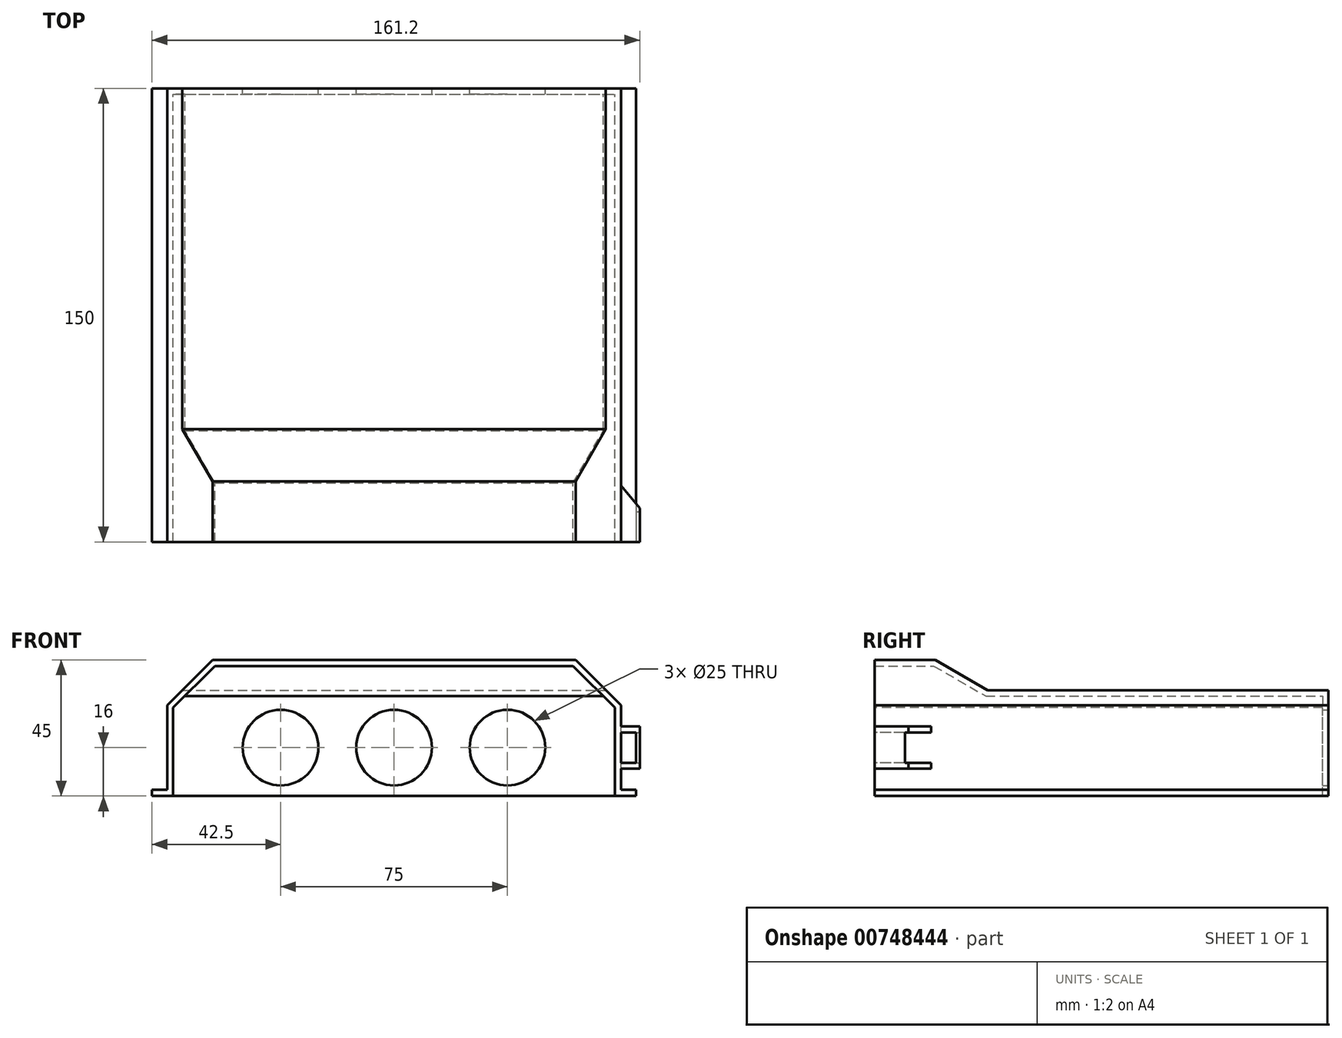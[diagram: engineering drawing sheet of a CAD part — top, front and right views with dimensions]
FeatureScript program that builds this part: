
annotation { "Feature Type Name" : "Feature", "Feature Type Description" : "" }
export const myFeature = defineFeature(function(context is Context, id is Id, definition is map)
    precondition{}
    {
        {
            var Q0;
            Q0=qCreatedBy(makeId("Front.planeOp"),FACE);
            var sketch = newSketch(context, id + "F0", { "sketchPlane" : qUnion([Q0])});
            skLineSegment(sketch, "E0.bottom", {"start": v(0, 0) * mm, "end": v(150, 0) * mm});
            skLineSegment(sketch, "E0.top", {"start": v(0, 45) * mm, "end": v(150, 45) * mm});
            skLineSegment(sketch, "E0.left", {"start": v(0, 0) * mm, "end": v(0, 45) * mm});
            skLineSegment(sketch, "E0.right", {"start": v(150, 0) * mm, "end": v(150, 45) * mm});
            skSolve(sketch);
        }
        {
            var Q0;
            Q0=qSketchRegion(id+"F0",true);
            extrude(context, id + "F1", {"entities" : qUnion([Q0]), "depth" : 150 * mm, "offsetDistance" : 25 * mm});
        }
        {
            var Q0;
            Q0=makeQuery(id+"F1.opExtrude","SWEPT_FACE",FACE,{"disambiguationData":[OSD([sQuery(id+"F0.wireOp",EDGE,"E0.bottom")])]});
            var sketch = newSketch(context, id + "F2", { "sketchPlane" : qUnion([Q0])});
            skLineSegment(sketch, "E1.0", {"start": v(150, 150) * mm, "end": v(150, 0) * mm});
            skLineSegment(sketch, "E2.0", {"start": v(0, 150) * mm, "end": v(0, 0) * mm});
            skLineSegment(sketch, "E3", {"start": v(0, 150) * mm, "end": v(-5, 150) * mm});
            skLineSegment(sketch, "E4", {"start": v(-5, 150) * mm, "end": v(-5, 0) * mm});
            skLineSegment(sketch, "E5", {"start": v(155, 0) * mm, "end": v(155, 150) * mm});
            skLineSegment(sketch, "E6", {"start": v(155, 150) * mm, "end": v(150, 150) * mm});
            skLineSegment(sketch, "E7", {"start": v(150, 0) * mm, "end": v(155, 0) * mm});
            skLineSegment(sketch, "E8", {"start": v(0.46, 0) * mm, "end": v(-5, 0) * mm});
            skSolve(sketch);
        }
        {
            var Q0;
            Q0=makeQuery(id+"F2.imprint","IMPRINT",FACE,{"disambiguationData":[TD([[makeQuery(id+"F2.imprint","IMPRINT",EDGE,{"derivedFrom":sQuery(id+"F2.wireOp",EDGE,"E1.0")}),1.0]])]});
            var Q1;
            {var subQ0=sQuery(id+"F2.wireOp",EDGE,"E2.0");Q1=makeQuery(id+"F2.imprint","IMPRINT",FACE,{"disambiguationData":[TD([[makeQuery(id+"F2.imprint","IMPRINT",EDGE,{"derivedFrom":subQ0}),-1.0]])]});}
            extrude(context, id + "F3", {"entities" : qUnion([Q0, Q1]), "operationType" : NewBodyOperationType.ADD, "oppositeDirection" : true, "depth" : 2 * mm, "offsetDistance" : 25 * mm});
        }
        {
            var Q0;
            Q0=makeQuery(id+"F1.opExtrude","SWEPT_FACE",FACE,{"disambiguationData":[OSD([sQuery(id+"F0.wireOp",EDGE,"E0.right")])]});
            var sketch = newSketch(context, id + "F4", { "sketchPlane" : qUnion([Q0])});
            skLineSegment(sketch, "E9", {"start": v(0, 45) * mm, "end": v(-130, 45) * mm});
            skLineSegment(sketch, "E10", {"start": v(-130, 45) * mm, "end": v(-112.68, 35) * mm});
            skLineSegment(sketch, "E11", {"start": v(-112.68, 35) * mm, "end": v(0, 35) * mm});
            skLineSegment(sketch, "E12", {"start": v(0, 35) * mm, "end": v(0, 45) * mm});
            skSolve(sketch);
        }
        {
            var Q0;
            Q0 = qSketchRegion(id + "F4", true);
            extrude(context, id + "F5", {"entities" : qUnion([Q0]), "operationType" : NewBodyOperationType.REMOVE, "endBound" : BoundingType.UP_TO_NEXT, "oppositeDirection" : true, "depth" : 25 * mm, "offsetDistance" : 25 * mm});
        }
        {
            var Q0;
            Q0=makeQuery(id+"FCt8RxKQ0T1Ob7Y_1.boolean.opBoolean","COPY",EDGE,{"derivedFrom":makeQuery(id+"FCt8RxKQ0T1Ob7Y_1.opExtrude","SWEPT_EDGE",EDGE,{"disambiguationData":[OSD([sQuery(id+"FIqywhC7vN5m6TC_1.wireOp",EDGE,"XllLzcVL-DN8Z-CTJ4-3NpV-jDezmlgxU65w.top"),sQuery(id+"FIqywhC7vN5m6TC_1.wireOp",EDGE,"XllLzcVL-DN8Z-CTJ4-3NpV-jDezmlgxU65w.left")])]})});
            var Q1;
            Q1=makeQuery(id+"FCt8RxKQ0T1Ob7Y_1.boolean.opBoolean","COPY",EDGE,{"derivedFrom":makeQuery(id+"FCt8RxKQ0T1Ob7Y_1.opExtrude","TWEAK_EDGE",EDGE,{"derivedFrom":[makeQuery(id+"F1.opExtrude","CAP_FACE",FACE,{"disambiguationData":[OSD([sQuery(id+"F0.wireOp",EDGE,"E0.bottom"),sQuery(id+"F0.wireOp",EDGE,"E0.top"),sQuery(id+"F0.wireOp",EDGE,"E0.left"),sQuery(id+"F0.wireOp",EDGE,"E0.right")])],"isStart":true}),makeQuery(id+"FIqywhC7vN5m6TC_1.imprint","IMPRINT",EDGE,{"derivedFrom":sQuery(id+"FIqywhC7vN5m6TC_1.wireOp",EDGE,"XllLzcVL-DN8Z-CTJ4-3NpV-jDezmlgxU65w.top")})]})});
            var Q2;
            Q2=makeQuery(id+"FCt8RxKQ0T1Ob7Y_1.boolean.opBoolean","COPY",EDGE,{"derivedFrom":makeQuery(id+"FCt8RxKQ0T1Ob7Y_1.opExtrude","SWEPT_EDGE",EDGE,{"disambiguationData":[OSD([sQuery(id+"FIqywhC7vN5m6TC_1.wireOp",EDGE,"XllLzcVL-DN8Z-CTJ4-3NpV-jDezmlgxU65w.top"),sQuery(id+"FIqywhC7vN5m6TC_1.wireOp",EDGE,"XllLzcVL-DN8Z-CTJ4-3NpV-jDezmlgxU65w.right")])]})});
            var Q3;
            Q3=makeQuery(id+"F1.opExtrude","SWEPT_EDGE",EDGE,{"disambiguationData":[OSD([sQuery(id+"F0.wireOp",EDGE,"E0.top"),sQuery(id+"F0.wireOp",EDGE,"E0.left")])]});
            var Q4;
            Q4=makeQuery(id+"F1.opExtrude","CAP_EDGE",EDGE,{"disambiguationData":[OSD([sQuery(id+"F0.wireOp",EDGE,"E0.top")])],"isStart":true});
            var Q5;
            Q5=makeQuery(id+"F1.opExtrude","SWEPT_EDGE",EDGE,{"disambiguationData":[OSD([sQuery(id+"F0.wireOp",EDGE,"E0.top"),sQuery(id+"F0.wireOp",EDGE,"E0.right")])]});
            chamfer(context, id + "F6", {"entities" : qUnion([Q0, Q1, Q2, Q3, Q4, Q5]), "width" : 15 * mm, "tangentPropagation" : true});
        }
        {
            var Q0;
            Q0=makeQuery(id+"F3.boolean.opBoolean","MERGE",FACE,{"derivedFrom":[makeQuery(id+"F1.opExtrude","CAP_FACE",FACE,{"disambiguationData":[OSD([sQuery(id+"F0.wireOp",EDGE,"E0.bottom"),sQuery(id+"F0.wireOp",EDGE,"E0.top"),sQuery(id+"F0.wireOp",EDGE,"E0.left"),sQuery(id+"F0.wireOp",EDGE,"E0.right")])],"isStart":false}),makeQuery(id+"F3.opExtrude","SWEPT_FACE",FACE,{"disambiguationData":[OSD([sQuery(id+"F2.wireOp",EDGE,"E3")])]}),makeQuery(id+"F3.opExtrude","SWEPT_FACE",FACE,{"disambiguationData":[OSD([sQuery(id+"F2.wireOp",EDGE,"E6")])]})]});
            var Q1;
            Q1=makeQuery(id+"F3.boolean.opBoolean","MERGE",FACE,{"derivedFrom":[makeQuery(id+"F1.opExtrude","SWEPT_FACE",FACE,{"disambiguationData":[OSD([sQuery(id+"F0.wireOp",EDGE,"E0.bottom")])]}),makeQuery(id+"F3.opExtrude","CAP_FACE",FACE,{"disambiguationData":[OSD([sQuery(id+"F2.wireOp",EDGE,"E1.0"),sQuery(id+"F2.wireOp",EDGE,"E5"),sQuery(id+"F2.wireOp",EDGE,"E6"),sQuery(id+"F2.wireOp",EDGE,"E7")])],"isStart":true}),makeQuery(id+"F3.opExtrude","CAP_FACE",FACE,{"disambiguationData":[OSD([sQuery(id+"F2.wireOp",EDGE,"E2.0"),sQuery(id+"F2.wireOp",EDGE,"E3"),sQuery(id+"F2.wireOp",EDGE,"E4"),sQuery(id+"F2.wireOp",EDGE,"E8")])],"isStart":true})]});
            shell(context, id + "F7", {"entities" : qUnion([Q0, Q1]), "thickness" : 2 * mm});
        }
        {
            var Q0;
            Q0=makeQuery(id+"F1.opExtrude","CAP_FACE",FACE,{"disambiguationData":[OSD([sQuery(id+"F0.wireOp",EDGE,"E0.bottom"),sQuery(id+"F0.wireOp",EDGE,"E0.top"),sQuery(id+"F0.wireOp",EDGE,"E0.left"),sQuery(id+"F0.wireOp",EDGE,"E0.right")])],"isStart":true});
            var sketch = newSketch(context, id + "F8", { "sketchPlane" : qUnion([Q0])});
            skLineSegment(sketch, "E13", {"start": v(-150, 16) * mm, "end": v(-112.5, 16) * mm, "construction": true});
            skCircle(sketch, "E14", {"center": v(-112.5, 16) * mm, "radius": 12.5 * mm});
            skLineSegment(sketch, "E15", {"start": v(-112.5, 16) * mm, "end": v(-75, 16) * mm, "construction": true});
            skLineSegment(sketch, "E16", {"start": v(-75, 16) * mm, "end": v(-37.5, 16) * mm, "construction": true});
            skLineSegment(sketch, "E17", {"start": v(-37.5, 16) * mm, "end": v(0, 16) * mm, "construction": true});
            skCircle(sketch, "E18", {"center": v(-75, 16) * mm, "radius": 12.5 * mm});
            skCircle(sketch, "E19", {"center": v(-37.5, 16) * mm, "radius": 12.5 * mm});
            skLineSegment(sketch, "E20", {"start": v(-75, 0) * mm, "end": v(-75, 16) * mm, "construction": true});
            skSolve(sketch);
        }
        {
            var Q0;
            Q0=makeQuery(id+"F8.imprint","IMPRINT",FACE,{"disambiguationData":[TD([[makeQuery(id+"F8.imprint","IMPRINT",EDGE,{"derivedFrom":sQuery(id+"F8.wireOp",EDGE,"E14")}),1.0]])]});
            var Q1;
            Q1=makeQuery(id+"F8.imprint","IMPRINT",FACE,{"disambiguationData":[TD([[makeQuery(id+"F8.imprint","IMPRINT",EDGE,{"derivedFrom":sQuery(id+"F8.wireOp",EDGE,"E18")}),1.0]])]});
            var Q2;
            Q2=makeQuery(id+"F8.imprint","IMPRINT",FACE,{"disambiguationData":[TD([[makeQuery(id+"F8.imprint","IMPRINT",EDGE,{"derivedFrom":sQuery(id+"F8.wireOp",EDGE,"E19")}),1.0]])]});
            extrude(context, id + "F9", {"entities" : qUnion([Q0, Q1, Q2]), "operationType" : NewBodyOperationType.REMOVE, "oppositeDirection" : true, "depth" : 25 * mm, "offsetDistance" : 25 * mm});
        }
        {
            var Q0;
            Q0=makeQuery(id+"F3.boolean.opBoolean","MERGE",FACE,{"derivedFrom":[makeQuery(id+"F1.opExtrude","CAP_FACE",FACE,{"disambiguationData":[OSD([sQuery(id+"F0.wireOp",EDGE,"E0.bottom"),sQuery(id+"F0.wireOp",EDGE,"E0.top"),sQuery(id+"F0.wireOp",EDGE,"E0.left"),sQuery(id+"F0.wireOp",EDGE,"E0.right")])],"isStart":false}),makeQuery(id+"F3.opExtrude","SWEPT_FACE",FACE,{"disambiguationData":[OSD([sQuery(id+"F2.wireOp",EDGE,"E3")])]}),makeQuery(id+"F3.opExtrude","SWEPT_FACE",FACE,{"disambiguationData":[OSD([sQuery(id+"F2.wireOp",EDGE,"E6")])]})]});
            var sketch = newSketch(context, id + "F10", { "sketchPlane" : qUnion([Q0])});
            skLineSegment(sketch, "E21.bottom", {"start": v(156.2, 23) * mm, "end": v(150, 23) * mm});
            skLineSegment(sketch, "E21.top", {"start": v(156.2, 9) * mm, "end": v(150, 9) * mm});
            skLineSegment(sketch, "E21.left", {"start": v(150, 23) * mm, "end": v(150, 21) * mm});
            skLineSegment(sketch, "E21.right", {"start": v(156.2, 23) * mm, "end": v(156.2, 9) * mm});
            skLineSegment(sketch, "E22.bottom", {"start": v(155, 21) * mm, "end": v(150, 21) * mm});
            skLineSegment(sketch, "E22.top", {"start": v(155, 11) * mm, "end": v(150, 11) * mm});
            skLineSegment(sketch, "E22.right", {"start": v(155, 21) * mm, "end": v(155, 11) * mm});
            skLineSegment(sketch, "E23.trimOffspring", {"start": v(150, 11) * mm, "end": v(150, 9) * mm});
            skLineSegment(sketch, "E24", {"start": v(155, 16) * mm, "end": v(150, 16) * mm, "construction": true});
            skSolve(sketch);
        }
        {
            var Q0;
            Q0=makeQuery(id+"F10.imprint","IMPRINT",FACE,{"disambiguationData":[TD([[makeQuery(id+"F10.imprint","IMPRINT",EDGE,{"derivedFrom":sQuery(id+"F10.wireOp",EDGE,"E21.bottom")}),1.0]])]});
            extrude(context, id + "F11", {"entities" : qUnion([Q0]), "operationType" : NewBodyOperationType.ADD, "oppositeDirection" : true, "depth" : 10 * mm, "offsetDistance" : 25 * mm});
        }
        {
            var Q0;
            Q0=makeQuery(id+"F11.opExtrude","SWEPT_FACE",FACE,{"disambiguationData":[OSD([sQuery(id+"F10.wireOp",EDGE,"E21.bottom")])]});
            var sketch = newSketch(context, id + "F12", { "sketchPlane" : qUnion([Q0])});
            skLineSegment(sketch, "E25", {"start": v(156.2, -140) * mm, "end": v(156.2, -138.8) * mm});
            skLineSegment(sketch, "E26", {"start": v(156.2, -138.8) * mm, "end": v(150, -131.41) * mm});
            skLineSegment(sketch, "E27", {"start": v(150, -140) * mm, "end": v(150, -131.41) * mm});
            skLineSegment(sketch, "E28", {"start": v(156.2, -140) * mm, "end": v(150, -140) * mm});
            skSolve(sketch);
        }
        {
            var Q0;
            Q0=makeQuery(id+"F12.imprint","IMPRINT",FACE,{"disambiguationData":[TD([[makeQuery(id+"F12.imprint","IMPRINT",EDGE,{"derivedFrom":sQuery(id+"F12.wireOp",EDGE,"E25")}),1.0]])]});
            var Q1;
            Q1=makeQuery(id+"F11.opExtrude","SWEPT_FACE",FACE,{"disambiguationData":[OSD([sQuery(id+"F10.wireOp",EDGE,"E21.top")])]});
            extrude(context, id + "F13", {"entities" : qUnion([Q0]), "operationType" : NewBodyOperationType.ADD, "endBound" : BoundingType.UP_TO_SURFACE, "oppositeDirection" : true, "depth" : 25 * mm, "endBoundEntityFace" : qUnion([Q1]), "offsetDistance" : 25 * mm});
        }
        {
            var Q0;
            Q0=makeQuery(id+"F11.boolean.opBoolean","MERGE",FACE,{"derivedFrom":[makeQuery(id+"F3.boolean.opBoolean","MERGE",FACE,{"derivedFrom":[makeQuery(id+"F1.opExtrude","CAP_FACE",FACE,{"disambiguationData":[OSD([sQuery(id+"F0.wireOp",EDGE,"E0.bottom"),sQuery(id+"F0.wireOp",EDGE,"E0.top"),sQuery(id+"F0.wireOp",EDGE,"E0.left"),sQuery(id+"F0.wireOp",EDGE,"E0.right")])],"isStart":false}),makeQuery(id+"F3.opExtrude","SWEPT_FACE",FACE,{"disambiguationData":[OSD([sQuery(id+"F2.wireOp",EDGE,"E3")])]}),makeQuery(id+"F3.opExtrude","SWEPT_FACE",FACE,{"disambiguationData":[OSD([sQuery(id+"F2.wireOp",EDGE,"E6")])]})]}),makeQuery(id+"F11.opExtrude","CAP_FACE",FACE,{"disambiguationData":[OSD([sQuery(id+"F10.wireOp",EDGE,"E21.bottom"),sQuery(id+"F10.wireOp",EDGE,"E21.top"),sQuery(id+"F10.wireOp",EDGE,"E21.left"),sQuery(id+"F10.wireOp",EDGE,"E21.right"),sQuery(id+"F10.wireOp",EDGE,"E22.bottom"),sQuery(id+"F10.wireOp",EDGE,"E22.top"),sQuery(id+"F10.wireOp",EDGE,"E22.right"),sQuery(id+"F10.wireOp",EDGE,"E23.trimOffspring")])],"isStart":true})]});
            var sketch = newSketch(context, id + "F14", { "sketchPlane" : qUnion([Q0])});
            skLineSegment(sketch, "E29.0", {"start": v(155, 21) * mm, "end": v(150, 21) * mm});
            skLineSegment(sketch, "E30.0", {"start": v(155, 11) * mm, "end": v(155, 21) * mm});
            skLineSegment(sketch, "E31.0", {"start": v(155, 11) * mm, "end": v(150, 11) * mm});
            skLineSegment(sketch, "E32.0", {"start": v(150, 11) * mm, "end": v(150, 21) * mm});
            skSolve(sketch);
        }
        {
            var Q0;
            Q0=makeQuery(id+"F14.imprint","IMPRINT",FACE,{"disambiguationData":[TD([[makeQuery(id+"F14.imprint","IMPRINT",EDGE,{"derivedFrom":sQuery(id+"F14.wireOp",EDGE,"E29.0")}),1.0]])]});
            extrude(context, id + "F15", {"entities" : qUnion([Q0]), "operationType" : NewBodyOperationType.REMOVE, "oppositeDirection" : true, "depth" : 25 * mm, "offsetDistance" : 25 * mm});
        }
        {
            var Q0;
            Q0=makeQuery(id+"F13.boolean.opBoolean","MERGE",FACE,{"derivedFrom":[makeQuery(id+"F11.opExtrude","SWEPT_FACE",FACE,{"disambiguationData":[OSD([sQuery(id+"F10.wireOp",EDGE,"E21.right")])]}),makeQuery(id+"F13.opExtrude","SWEPT_FACE",FACE,{"disambiguationData":[OSD([sQuery(id+"F12.wireOp",EDGE,"E25")])]})]});
            var sketch = newSketch(context, id + "F16", { "sketchPlane" : qUnion([Q0])});
            skPoint(sketch, "E33.0", {"position": v(-137.37, 16) * mm});
            skLineSegment(sketch, "E34.0", {"start": v(-137.37, 11) * mm, "end": v(-137.37, 21) * mm, "construction": true});
            skLineSegment(sketch, "E35.bottom", {"start": v(-140, 11) * mm, "end": v(-137.37, 11) * mm});
            skLineSegment(sketch, "E35.top", {"start": v(-140, 21) * mm, "end": v(-137.37, 21) * mm});
            skLineSegment(sketch, "E35.left", {"start": v(-137.37, 11) * mm, "end": v(-137.37, 21) * mm});
            skLineSegment(sketch, "E35.right", {"start": v(-140, 21) * mm, "end": v(-140, 11) * mm});
            skSolve(sketch);
        }
        {
            var Q0;
            {var subQ0=sQuery(id+"F16.wireOp",EDGE,"E35.right");Q0=makeQuery(id+"F16.imprint","IMPRINT",FACE,{"disambiguationData":[TD([[makeQuery(id+"F16.imprint","IMPRINT",EDGE,{"derivedFrom":subQ0}),1.0]])]});}
            var Q1;
            {var subQ0=sQuery(id+"F16.wireOp",EDGE,"E35.left");Q1=makeQuery(id+"F16.imprint","IMPRINT",FACE,{"disambiguationData":[TD([[makeQuery(id+"F16.imprint","IMPRINT",EDGE,{"derivedFrom":subQ0}),1.0]])]});}
            var Q2;
            {var subQ1=sQuery(id+"F10.wireOp",EDGE,"E22.bottom");var subQ8=sQuery(id+"F0.wireOp",EDGE,"E0.right");var subQ14=makeQuery(id+"F1.opExtrude","SWEPT_FACE",FACE,{"disambiguationData":[OSD([subQ8])]});var subQ15=sQuery(id+"F2.wireOp",EDGE,"E7");Q2=makeQuery(id+"F15.boolean.opBoolean","MERGE",FACE,{"derivedFrom":[makeQuery(id+"F13.boolean.opBoolean","SPLIT",FACE,{"disambiguationData":[TD([makeQuery(id+"F3.opExtrude","SWEPT_FACE",FACE,{"disambiguationData":[OSD([subQ15])]})])],"derivedFrom":subQ14}),makeQuery(id+"F13.boolean.opBoolean","SPLIT",FACE,{"disambiguationData":[TD([makeQuery(id+"F11.opExtrude","SWEPT_FACE",FACE,{"disambiguationData":[OSD([subQ1])]})])],"derivedFrom":subQ14})],"fromTools":[makeQuery(id+"F15.opExtrude","SWEPT_FACE",FACE,{"disambiguationData":[OSD([sQuery(id+"F14.wireOp",EDGE,"E32.0")])]})]});}
            extrude(context, id + "F17", {"entities" : qUnion([Q0, Q1]), "operationType" : NewBodyOperationType.REMOVE, "endBound" : BoundingType.UP_TO_SURFACE, "oppositeDirection" : true, "depth" : 25 * mm, "endBoundEntityFace" : qUnion([Q2]), "offsetDistance" : 25 * mm});
        }
    });
